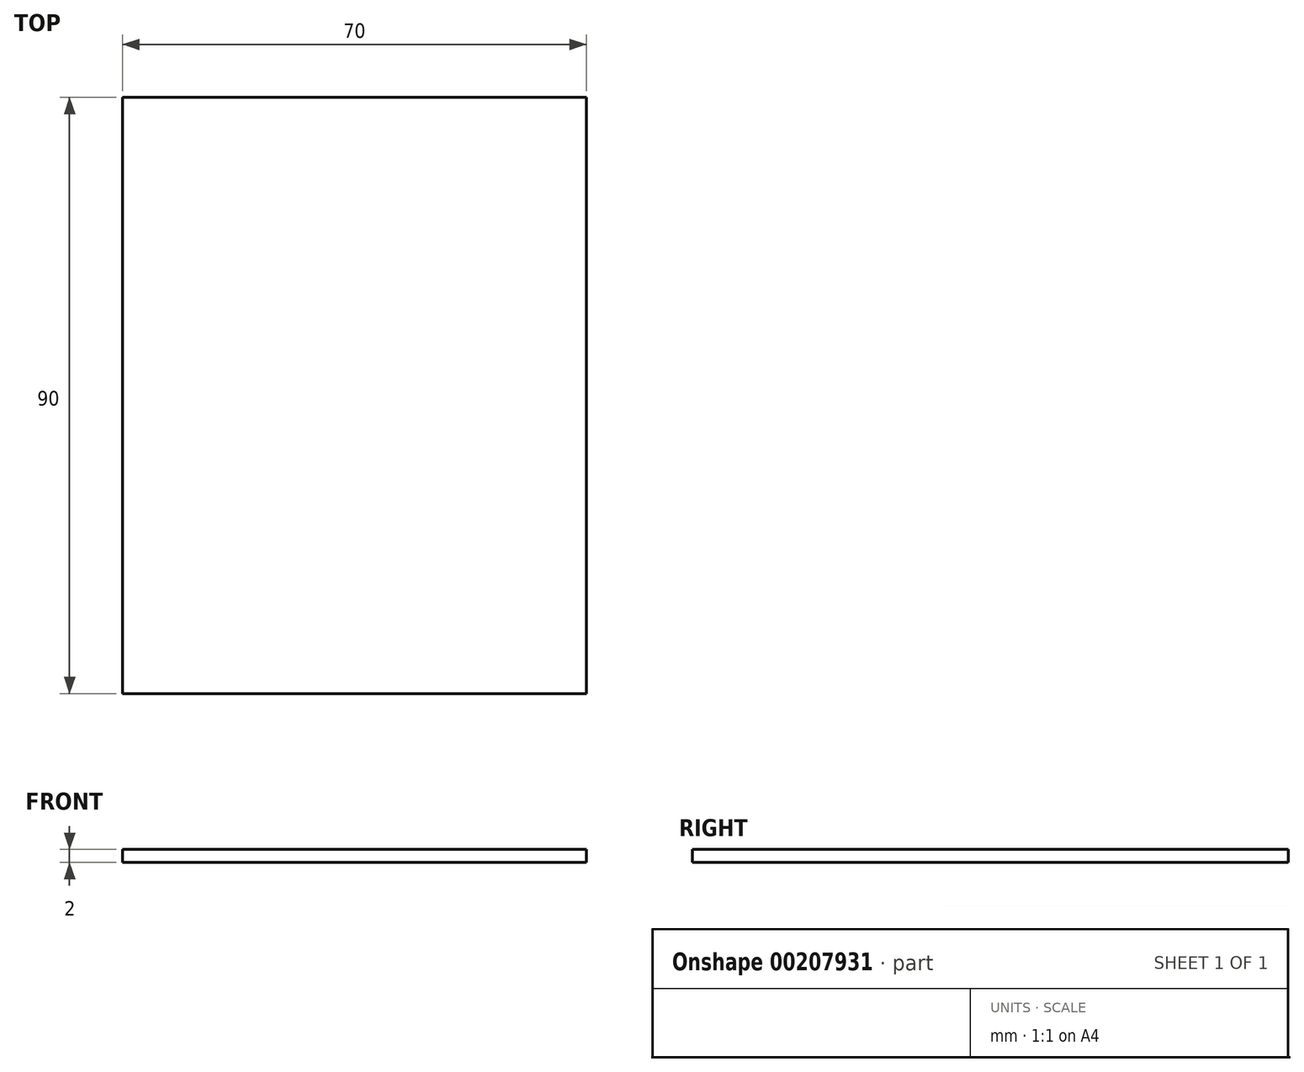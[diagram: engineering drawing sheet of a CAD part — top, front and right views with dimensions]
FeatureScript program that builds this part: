
annotation { "Feature Type Name" : "Feature", "Feature Type Description" : "" }
export const myFeature = defineFeature(function(context is Context, id is Id, definition is map)
    precondition{}
    {
        {
            var Q0;
            Q0=qCreatedBy(makeId("Top.planeOp"),FACE);
            var sketch = newSketch(context, id + "F0", { "sketchPlane" : qUnion([Q0])});
            skLineSegment(sketch, "E0.bottom", {"start": v(35.19, -44.12) * mm, "end": v(-34.81, -44.12) * mm});
            skLineSegment(sketch, "E0.top", {"start": v(35.19, 45.88) * mm, "end": v(-34.81, 45.88) * mm});
            skLineSegment(sketch, "E0.left", {"start": v(35.19, -44.12) * mm, "end": v(35.19, 45.88) * mm});
            skLineSegment(sketch, "E0.right", {"start": v(-34.81, -44.12) * mm, "end": v(-34.81, 45.88) * mm});
            skPoint(sketch, "E0.middle", {"position": v(-47.41, 32.88) * mm});
            skSolve(sketch);
        }
        {
            var Q0;
            Q0=makeQuery(id+"F0.imprint","IMPRINT",FACE,{"disambiguationData":[TD([[makeQuery(id+"F0.imprint","IMPRINT",EDGE,{"derivedFrom":sQuery(id+"F0.wireOp",EDGE,"E0.bottom")}),-1.0]])]});
            extrude(context, id + "F1", {"entities" : qUnion([Q0]), "depth" : 2 * mm});
        }
    });
